# Revit family: MYRAL 3500-xxx-F-x
name_source: partatom
category: Oprawy oświetleniowe
units: mm (PartAtom-declared; Revit-internal decimal feet)

## family parameters
Numer OmniClass = 23.80.70.11
Obiekt nadrzędny = Powierzchnia
Punkt obliczania pomieszczeń = Nie
Tnij formami wycięć po wczytaniu = Nie
Typ części = Normalny
Tytuł OmniClass = Luminaries for Internal Lighting
Współdzielony = Nie
Wymiar okrągłego złącza = Użyj średnicy
Źródło światła = Tak

## types (4) — shared parameters
Emituj kształt widoczny w renderingu = Nie
Emituj ze średnicy okręgu = 99 mm  [stored 0.324803 ft]
Filtr koloru = 16777215
Kod zespołu = D5020200
Lampa = LED
Obciążenie pozorne = 29 VA
Odchylenie kierunku = 90.00°
Plik sieci fotometrycznej = MYRAL xxx-F.IES
Producent = RIDI Leuchten GmbH
URL = https://www.spectral-lighting.com
Zmiana temperatury barwowej przyciemniania lampy = <Brak>
brand = Spectral
conformity mark = CE
electrical safety class = 1
height = 93 mm  [stored 0.305118 ft]
ingress protection (IP) code = IP20
length = 120 mm  [stored 0.393701 ft]
nominal frequency = 50-60Hz
nominal voltage = 230
rated input power = 29
voltage type (AC, DC, UC) = AC
weight = 0,6 kg
width = 120 mm  [stored 0.393701 ft]
zero-valued in all types: Domyślna rzędna

## per-type parameters (varying)
| type | Model |
| MYRAL 3500-830-F | SPG0320186 |
| MYRAL 3500-830-F-DALI | SPG0330186 |
| MYRAL 3500-840-F | SPG0320187 |
| MYRAL 3500-840-F-DALI | SPG0330187 |

note: column(s) folded — value = type name in every type: product name

note: [stored X ft] marks values corroborated as IEEE doubles in the binary element streams (Revit-internal decimal feet)
